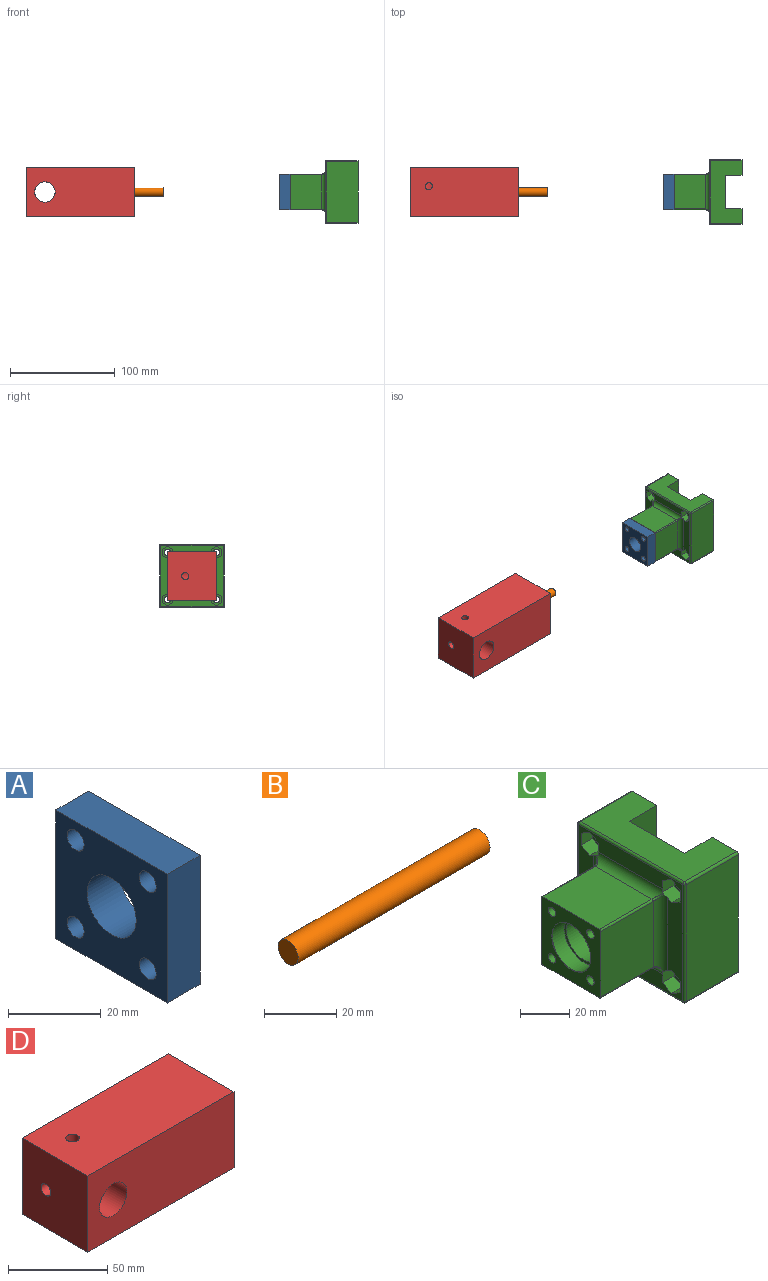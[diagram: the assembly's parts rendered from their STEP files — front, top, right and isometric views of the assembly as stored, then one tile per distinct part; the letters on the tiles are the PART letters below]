
ASSEMBLY  parts=4 mates=7
PART A: 11 faces, bbox 10x34x34 mm
  f0: plane 34x10mm, normal (0,0,1), area 340mm2, adj f1,f8,f9,f10
  f1: plane 34x10mm, normal (0,1,0), area 340mm2, adj f0,f2,f9,f10
  f2: plane 34x10mm, normal (0,0,-1), area 340mm2, adj f1,f8,f9,f10
  f3: cylinder r=2.6mm len=10mm, axis (1,0,0), area 163.4mm2, adj f9,f10
  f4: cylinder r=2.6mm len=10mm, axis (1,0,0), area 163.4mm2, adj f9,f10
  f5: cylinder r=2.6mm len=10mm, axis (1,0,0), area 163.4mm2, adj f9,f10
  f6: cylinder r=2.6mm len=10mm, axis (1,0,0), area 163.4mm2, adj f9,f10
  f7: cylinder r=7.5mm len=15mm, axis (1,0,0), area 471.2mm2, adj f9,f10
  f8: plane 34x10mm, normal (0,-1,0), area 340mm2, adj f0,f2,f9,f10
  f9: plane 34x34mm, normal (-1,0,0), area 894.3mm2, adj f0,f1,f2,f3,f4,f5,f6,f7
  f10: plane 34x34mm, normal (1,0,0), area 894.3mm2, adj f0,f1,f2,f3,f4,f5,f6,f7
PART B: 3 faces, bbox 75x7.9x7.9 mm
  f0: cylinder r=3.95mm len=75mm, axis (-1,0,0), area 1861.4mm2, adj f1,f2
  f1: plane 7.9x7.9mm, normal (1,0,0), area 49mm2, adj f0
  f2: plane 7.9x7.9mm, normal (-1,0,0), area 49mm2, adj f0
PART C: 84 faces, bbox 64.9x61.8x60 mm
  f0: plane 59.75x58mm, normal (-1,0,0), area 1377.6mm2, adj f15,f16,f17,f18,f19,f20,f22,f23
  f1: plane 60x15mm, normal (1,0,0), area 837.2mm2, adj f3,f5,f6,f8,f9,f11,f64,f66
  f2: plane 60x15mm, normal (1,0,0), area 837.2mm2, adj f4,f5,f6,f7,f10,f12,f63,f65
  f3: cylinder r=3.15mm len=24.38mm, axis (1,0,0), area 482.4mm2, adj f1,f28
  f4: cylinder r=3.15mm len=24.38mm, axis (1,0,0), area 482.4mm2, adj f2,f14
  f5: plane 59.75x29.88mm, normal (0,0,1), area 1281mm2, adj f1,f2,f9,f10,f13,f65,f66,f67
  f6: plane 59.75x29.88mm, normal (0,0,-1), area 1281mm2, adj f1,f2,f9,f10,f13,f63,f64,f74
  f7: plane 58x29.88mm, normal (0,1,0), area 1732.8mm2, adj f2,f63,f65,f70
  f8: plane 58x29.88mm, normal (0,-1,0), area 1732.8mm2, adj f1,f64,f66,f71
  f9: plane 60x15.88mm, normal (0,1,0), area 952.5mm2, adj f1,f5,f6,f13
  f10: plane 60x15.88mm, normal (0,-1,0), area 952.5mm2, adj f2,f5,f6,f13
  f11: cylinder r=3.15mm len=24.38mm, axis (1,0,0), area 482.4mm2, adj f1,f21
  f12: cylinder r=3.15mm len=24.38mm, axis (1,0,0), area 482.4mm2, adj f2,f35
  f13: plane 60x31.75mm, normal (1,0,0), area 1905mm2, adj f5,f6,f9,f10
  f14: plane 11.55x10mm, normal (-1,0,0), area 55.4mm2, adj f4,f15,f16,f17,f18,f19,f20
  f15: plane 6.5x5mm, normal (0,-0.5,-0.87), area 37.5mm2, adj f0,f14,f16,f20
  f16: plane 6.5x5mm, normal (0,0.5,-0.87), area 37.5mm2, adj f0,f14,f15,f17
  f17: plane 6.75x5.77mm, normal (0,1,0), area 37.6mm2, adj f0,f14,f16,f18,f48
  f18: plane 6.93x5.02mm, normal (0,0.5,0.87), area 38.1mm2, adj f0,f14,f17,f19,f48,f50,f78
  f19: plane 6.5x5mm, normal (0,-0.5,0.87), area 37.5mm2, adj f0,f14,f18,f20
  f20: plane 6.5x5.77mm, normal (0,-1,0), area 37.5mm2, adj f0,f14,f15,f19
  f21: plane 11.55x10mm, normal (-1,0,0), area 55.4mm2, adj f11,f22,f23,f24,f25,f26,f27
  f22: plane 6.5x5mm, normal (0,-0.5,-0.87), area 37.5mm2, adj f0,f21,f23,f27
  f23: plane 6.5x5mm, normal (0,0.5,-0.87), area 37.5mm2, adj f0,f21,f22,f24
  f24: plane 6.5x5.77mm, normal (0,1,0), area 37.5mm2, adj f0,f21,f23,f25
  f25: plane 6.5x5mm, normal (0,0.5,0.87), area 37.5mm2, adj f0,f21,f24,f26
  f26: plane 6.93x5.02mm, normal (0,-0.5,0.87), area 38.1mm2, adj f0,f21,f25,f27,f47,f48,f76
  f27: plane 6.75x5.77mm, normal (0,-1,0), area 37.6mm2, adj f0,f21,f22,f26,f48
  f28: plane 11.55x10mm, normal (-1,0,0), area 55.4mm2, adj f3,f29,f30,f31,f32,f33,f34
  f29: plane 6.5x5mm, normal (0,0.5,0.87), area 37.5mm2, adj f0,f28,f30,f34
  f30: plane 6.5x5mm, normal (0,-0.5,0.87), area 37.5mm2, adj f0,f28,f29,f31
  f31: plane 6.75x5.77mm, normal (0,-1,0), area 37.6mm2, adj f0,f28,f30,f32,f49
  f32: plane 6.93x5.02mm, normal (0,-0.5,-0.87), area 38.1mm2, adj f0,f28,f31,f33,f47,f49,f80
  f33: plane 6.5x5mm, normal (0,0.5,-0.87), area 37.5mm2, adj f0,f28,f32,f34
  f34: plane 6.5x5.77mm, normal (0,1,0), area 37.5mm2, adj f0,f28,f29,f33
  f35: plane 11.55x10mm, normal (-1,0,0), area 55.4mm2, adj f12,f36,f37,f38,f39,f40,f41
  f36: plane 6.5x5mm, normal (0,0.5,0.87), area 37.5mm2, adj f0,f35,f37,f41
  f37: plane 6.5x5mm, normal (0,-0.5,0.87), area 37.5mm2, adj f0,f35,f36,f38
  f38: plane 6.5x5.77mm, normal (0,-1,0), area 37.5mm2, adj f0,f35,f37,f39
  f39: plane 6.5x5mm, normal (0,-0.5,-0.87), area 37.5mm2, adj f0,f35,f38,f40
  f40: plane 6.93x5.02mm, normal (0,0.5,-0.87), area 38.1mm2, adj f0,f35,f39,f41,f49,f50,f82
  f41: plane 6.75x5.77mm, normal (0,1,0), area 37.6mm2, adj f0,f35,f36,f40,f49
  f42: plane 32.5x30mm, normal (0,1,0), area 975mm2, adj f46,f50,f77,f81
  f43: plane 32.5x30mm, normal (0,0,-1), area 975mm2, adj f46,f49,f79,f81
  f44: plane 32.5x30mm, normal (0,-1,0), area 975mm2, adj f46,f47,f75,f79
  f45: plane 32.5x30mm, normal (0,0,1), area 975mm2, adj f46,f48,f75,f77
  f46: plane 34x34mm, normal (-1,0,0), area 711.3mm2, adj f42,f43,f44,f45,f55,f57,f59,f61
  f47: cylinder r=4mm len=38.09mm, axis (0,0,-1), area 224.9mm2, adj f0,f26,f32,f44,f76,f80
  f48: cylinder r=4mm len=37.91mm, axis (0,-1,0), area 220.5mm2, adj f0,f17,f18,f26,f27,f45,f76,f78
  f49: cylinder r=4mm len=37.91mm, axis (0,1,0), area 220.5mm2, adj f0,f31,f32,f40,f41,f43,f80,f82
  f50: cylinder r=4mm len=38.09mm, axis (0,0,1), area 224.9mm2, adj f0,f18,f40,f42,f78,f82
  f51: plane 22.05x22.05mm, normal (-1,0,0), area 77.1mm2, adj f52,f53
  f52: cylinder r=11.03mm len=22.05mm, axis (-1,0,0), area 484.9mm2, adj f51,f83
  f53: cylinder r=9.85mm len=39.5mm, axis (-1,0,0), area 2444.6mm2, adj f51,f54
  f54: plane 19.7x19.7mm, normal (-1,0,0), area 304.8mm2, adj f53
  f55: cylinder r=2.1mm len=11mm, axis (-1,0,0), area 145.1mm2, adj f46,f56
  f56: plane 4.2x4.2mm, normal (-1,0,0), area 13.9mm2, adj f55
  f57: cylinder r=2.1mm len=11mm, axis (-1,0,0), area 145.1mm2, adj f46,f58
  f58: plane 4.2x4.2mm, normal (-1,0,0), area 13.9mm2, adj f57
  f59: cylinder r=2.1mm len=11mm, axis (-1,0,0), area 145.1mm2, adj f46,f60
  f60: plane 4.2x4.2mm, normal (-1,0,0), area 13.9mm2, adj f59
  f61: cylinder r=2.1mm len=11mm, axis (-1,0,0), area 145.1mm2, adj f46,f62
  f62: plane 4.2x4.2mm, normal (-1,0,0), area 13.9mm2, adj f61
  f63: cylinder r=1mm len=29.88mm, axis (-1,0,0), area 46.9mm2, adj f2,f6,f7,f72
  f64: cylinder r=1mm len=29.88mm, axis (1,0,0), area 46.9mm2, adj f1,f6,f8,f73
  f65: cylinder r=1mm len=29.88mm, axis (1,0,0), area 46.9mm2, adj f2,f5,f7,f68
  f66: cylinder r=1mm len=29.88mm, axis (-1,0,0), area 46.9mm2, adj f1,f5,f8,f69
  f67: cylinder r=1mm len=59.75mm, axis (0,1,0), area 93.9mm2, adj f0,f5,f68,f69
  f68: sphere r=1mm, area 2.1mm2, adj f65,f67,f70
  f69: sphere r=1mm, area 1.6mm2, adj f66,f67,f71
  f70: cylinder r=1mm len=58mm, axis (0,0,-1), area 91.1mm2, adj f0,f7,f68,f72
  f71: cylinder r=1mm len=58mm, axis (0,0,-1), area 91.1mm2, adj f0,f8,f69,f73
  f72: sphere r=1mm, area 1mm2, adj f63,f70,f74
  f73: sphere r=1mm, area 1.6mm2, adj f64,f71,f74
  f74: cylinder r=1mm len=59.75mm, axis (0,-1,0), area 93.9mm2, adj f0,f6,f72,f73
  f75: cylinder r=0.75mm len=30mm, axis (1,0,0), area 35.3mm2, adj f44,f45,f46,f76
  f76: bspline ~4.27x3.34mm, area 4.7mm2, adj f26,f47,f48,f75
  f77: cylinder r=0.75mm len=30mm, axis (1,0,0), area 35.3mm2, adj f42,f45,f46,f78
  f78: bspline ~4.27x3.34mm, area 4.7mm2, adj f18,f48,f50,f77
  f79: cylinder r=0.75mm len=30mm, axis (1,0,0), area 35.3mm2, adj f43,f44,f46,f80
  f80: bspline ~3.88x3.34mm, area 4.7mm2, adj f32,f47,f49,f79
  f81: cylinder r=0.75mm len=30mm, axis (1,0,0), area 35.3mm2, adj f42,f43,f46,f82
  f82: bspline ~3.88x3.34mm, area 4.7mm2, adj f40,f49,f50,f81
  f83: cone r=11.03mm half-angle=45deg, axis (-1,0,0), area 9.8mm2, adj f46,f52
PART D: 16 faces, bbox 104x47x47 mm
  f0: plane 35x28mm, normal (0,0,-1), area 980mm2, adj f1,f3,f8,f9
  f1: plane 35x28mm, normal (0,1,0), area 980mm2, adj f0,f2,f8,f9
  f2: plane 35x28mm, normal (0,0,1), area 980mm2, adj f1,f3,f8,f9
  f3: plane 35x28mm, normal (0,-1,0), area 980mm2, adj f0,f2,f8,f9
  f4: plane 104x47mm, normal (0,0,-1), area 4888mm2, adj f5,f7,f8,f10
  f5: plane 104x47mm, normal (0,-1,0), area 4589.4mm2, adj f4,f6,f8,f10,f11
  f6: plane 104x47mm, normal (0,0,1), area 4851.7mm2, adj f5,f7,f8,f10,f13
  f7: plane 104x47mm, normal (0,1,0), area 4589.4mm2, adj f4,f6,f8,f10,f11
  f8: plane 47x47mm, normal (1,0,0), area 984mm2, adj f0,f1,f2,f3,f4,f5,f6,f7
  f9: plane 35x35mm, normal (1,0,0), area 1174.7mm2, adj f0,f1,f2,f3,f14
  f10: plane 47x47mm, normal (-1,0,0), area 2172.7mm2, adj f4,f5,f6,f7,f12
  f11: cylinder r=9.75mm len=47mm, axis (0,1,0), area 2805.7mm2, adj f5,f7,f12,f13
  f12: cylinder r=3.4mm len=8.86mm, axis (-1,0,0), area 182.7mm2, adj f10,f11
  f13: cylinder r=3.4mm len=14.36mm, axis (0,0,1), area 300.2mm2, adj f6,f11
  f14: cylinder r=4mm len=20mm, axis (1,0,0), area 502.7mm2, adj f9,f15
  f15: plane 8x8mm, normal (1,0,0), area 50.3mm2, adj f14
PLACE A rot(axis=(1,0,0),0deg) t=(0.87,-5.2,9.65)mm
PLACE B t=(-283.27,-9.49,33.3)mm
PLACE C t=(-22.45,-9.49,3.3)mm fixed
PLACE D t=(-164.94,0,0)mm
MATE cylindrical A.f7 <-> B.f0  axis (1,0,0) through (-97.33,-9.49,33.3)mm
MATE planar C.f42 <-> A.f1  axis (0,1,0) through (-72.33,7.51,33.3)mm
MATE planar C.f46 <-> A.f10  axis (-1,0,0) through (-87.33,-9.49,33.26)mm
MATE parallel D.f7 <-> C.f42  axis (0,1,0) through (-285.06,14.01,33.3)mm
MATE cylindrical D.f14 <-> B.f0  axis (1,0,0) through (-263.27,-9.49,33.3)mm
MATE planar D.f14 <-> B.f0  axis (1,0,0) through (-283.27,-9.49,33.3)mm
MATE cylindrical A.f3 <-> C.f59  axis (1,0,0) through (-97.33,-20.49,22.3)mm
